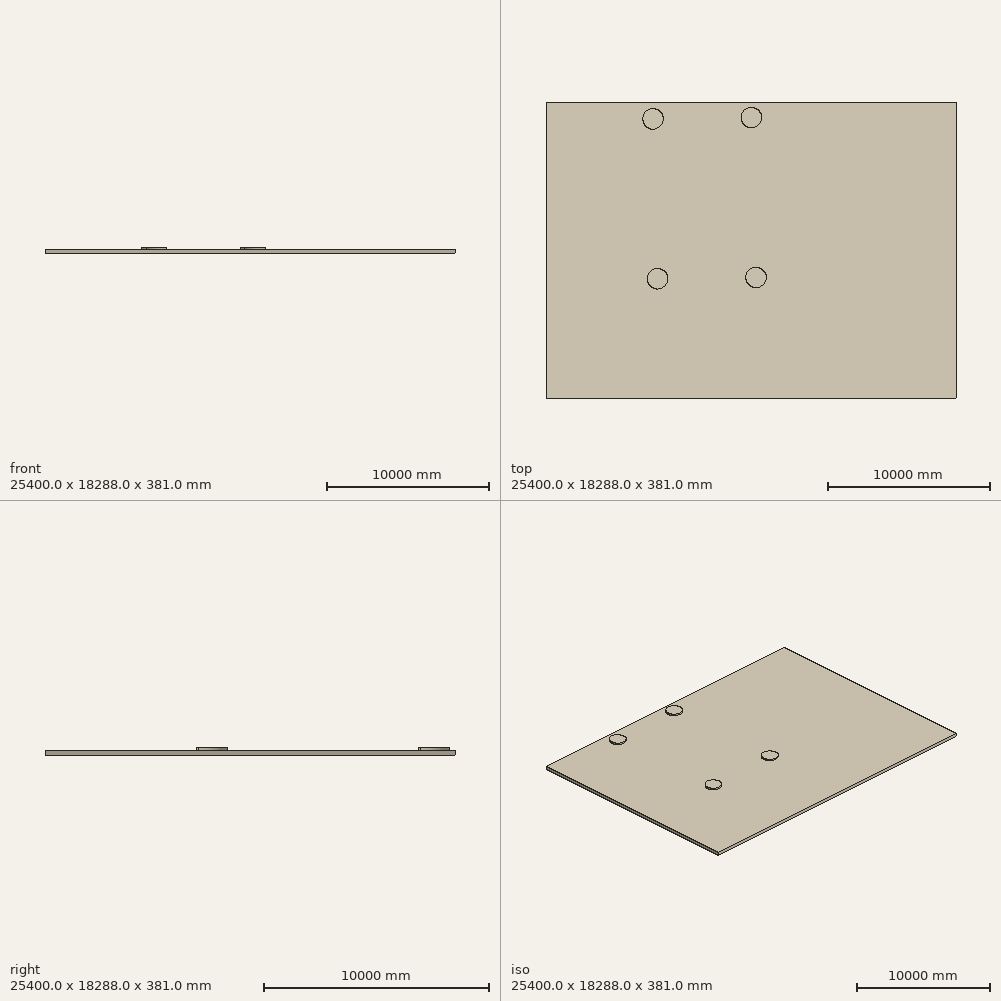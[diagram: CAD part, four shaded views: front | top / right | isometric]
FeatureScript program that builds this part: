
annotation { "Feature Type Name" : "Feature", "Feature Type Description" : "" }
export const myFeature = defineFeature(function(context is Context, id is Id, definition is map)
    precondition{}
    {
        {
            var Q0;
            Q0=qCreatedBy(makeId("Top.planeOp"),FACE);
            var sketch = newSketch(context, id + "F0", { "sketchPlane" : qUnion([Q0])});
            skLineSegment(sketch, "E0.bottom", {"start": v(12700, -9144) * mm, "end": v(-12700, -9144) * mm});
            skLineSegment(sketch, "E0.top", {"start": v(12700, 9144) * mm, "end": v(-12700, 9144) * mm});
            skLineSegment(sketch, "E0.left", {"start": v(12700, -9144) * mm, "end": v(12700, 9144) * mm});
            skLineSegment(sketch, "E0.right", {"start": v(-12700, -9144) * mm, "end": v(-12700, 9144) * mm});
            skPoint(sketch, "E0.middle", {"position": v(0, 0) * mm});
            skSolve(sketch);
        }
        {
            var Q0;
            Q0 = qSketchRegion(id + "F0", true);
            extrude(context, id + "F1", {"entities" : qUnion([Q0]), "depth" : 254 * mm, "offsetDistance" : 25.4 * mm});
        }
        {
            var Q0;
            Q0=makeQuery(id+"F1.opExtrude","CAP_FACE",FACE,{"disambiguationData":[OSD([sQuery(id+"F0.wireOp",EDGE,"E0.bottom"),sQuery(id+"F0.wireOp",EDGE,"E0.top"),sQuery(id+"F0.wireOp",EDGE,"E0.left"),sQuery(id+"F0.wireOp",EDGE,"E0.right")])],"isStart":false});
            var sketch = newSketch(context, id + "F2", { "sketchPlane" : qUnion([Q0])});
            skCircle(sketch, "E1", {"center": v(-6095.52, 8147.58) * mm, "radius": 635 * mm});
            skCircle(sketch, "E2", {"center": v(-5809.98, -1754.3) * mm, "radius": 635 * mm});
            skCircle(sketch, "E3", {"center": v(0, 8224.38) * mm, "radius": 635 * mm});
            skCircle(sketch, "E4", {"center": v(285.53, -1677.5) * mm, "radius": 635 * mm});
            skSolve(sketch);
        }
        {
            var Q0;
            Q0 = qSketchRegion(id + "F2", true);
            extrude(context, id + "F3", {"entities" : qUnion([Q0]), "operationType" : NewBodyOperationType.ADD, "depth" : 127 * mm, "offsetDistance" : 25.4 * mm});
        }
    });
